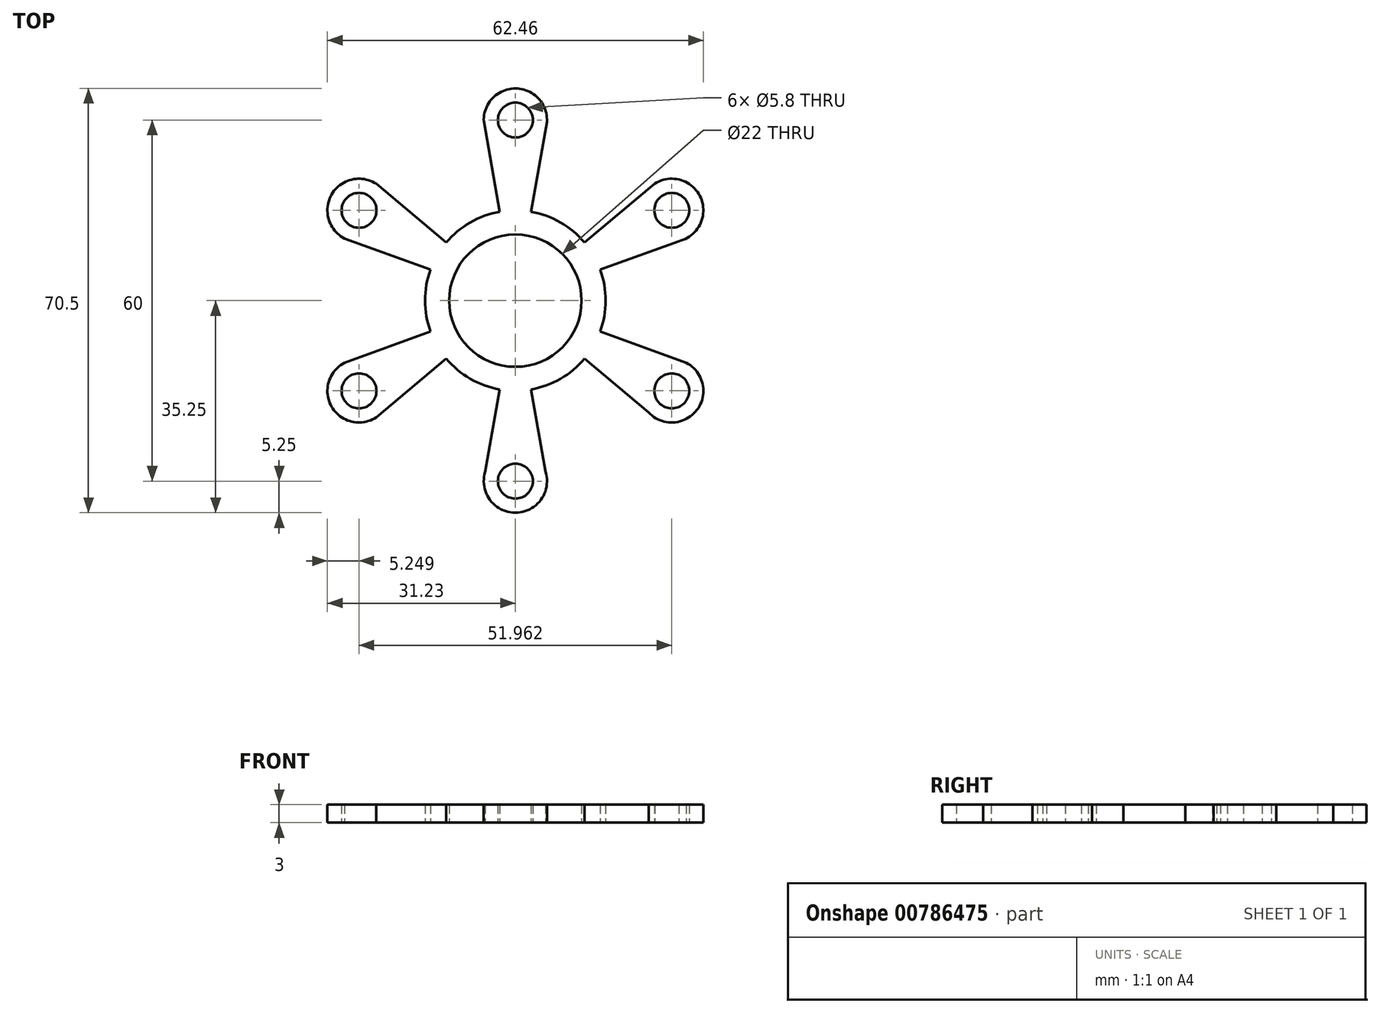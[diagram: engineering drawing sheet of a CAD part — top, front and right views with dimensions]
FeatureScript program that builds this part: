
annotation { "Feature Type Name" : "Feature", "Feature Type Description" : "" }
export const myFeature = defineFeature(function(context is Context, id is Id, definition is map)
    precondition{}
    {
        {
            var Q0;
            Q0=qCreatedBy(makeId("Top.planeOp"),FACE);
            var sketch = newSketch(context, id + "F0", { "sketchPlane" : qUnion([Q0])});
            skArc(sketch, "E0", {"start": v(-2.6, 14.77) * mm, "mid": v(-5.13, 14.1) * mm, "end": v(-7.5, 13) * mm});
            skLineSegment(sketch, "E1", {"start": v(2.6, 14.77) * mm, "end": v(5.25, 29.75) * mm});
            skArc(sketch, "E2", {"start": v(5.25, 29.75) * mm, "mid": v(0, 35.25) * mm, "end": v(-5.25, 29.75) * mm});
            skLineSegment(sketch, "E3.trimOffspring", {"start": v(-2.6, 14.77) * mm, "end": v(-5.25, 29.75) * mm});
            skArc(sketch, "E4.trimOffspring", {"start": v(7.5, 13) * mm, "mid": v(5.13, 14.1) * mm, "end": v(2.6, 14.77) * mm});
            skArc(sketch, "E5.1.0", {"start": v(-23.14, 19.42) * mm, "mid": v(-30.53, 17.63) * mm, "end": v(-28.38, 10.33) * mm});
            skLineSegment(sketch, "E5.1.1", {"start": v(-11.5, 9.64) * mm, "end": v(-23.14, 19.42) * mm});
            skArc(sketch, "E5.1.2", {"start": v(-7.5, 13) * mm, "mid": v(-9.64, 11.5) * mm, "end": v(-11.5, 9.64) * mm});
            skLineSegment(sketch, "E5.1.3", {"start": v(-14.1, 5.13) * mm, "end": v(-28.38, 10.33) * mm});
            skArc(sketch, "E5.1.4", {"start": v(-14.1, 5.13) * mm, "mid": v(-14.77, 2.6) * mm, "end": v(-15, 0) * mm});
            skArc(sketch, "E5.2.0", {"start": v(-28.38, -10.33) * mm, "mid": v(-30.53, -17.63) * mm, "end": v(-23.14, -19.42) * mm});
            skLineSegment(sketch, "E5.2.1", {"start": v(-14.1, -5.13) * mm, "end": v(-28.38, -10.33) * mm});
            skArc(sketch, "E5.2.2", {"start": v(-15, 0) * mm, "mid": v(-14.77, -2.6) * mm, "end": v(-14.1, -5.13) * mm});
            skLineSegment(sketch, "E5.2.3", {"start": v(-11.5, -9.64) * mm, "end": v(-23.14, -19.42) * mm});
            skArc(sketch, "E5.2.4", {"start": v(-11.5, -9.64) * mm, "mid": v(-9.64, -11.5) * mm, "end": v(-7.5, -13) * mm});
            skArc(sketch, "E5.3.0", {"start": v(-5.02, -28.44) * mm, "mid": v(0, -35.25) * mm, "end": v(5.02, -28.44) * mm});
            skLineSegment(sketch, "E5.3.1", {"start": v(-2.6, -14.77) * mm, "end": v(-5.02, -28.44) * mm});
            skArc(sketch, "E5.3.2", {"start": v(-7.5, -13) * mm, "mid": v(-5.13, -14.1) * mm, "end": v(-2.6, -14.77) * mm});
            skLineSegment(sketch, "E5.3.3", {"start": v(2.6, -14.77) * mm, "end": v(5.02, -28.44) * mm});
            skArc(sketch, "E5.3.4", {"start": v(2.6, -14.77) * mm, "mid": v(5.13, -14.1) * mm, "end": v(7.5, -13) * mm});
            skArc(sketch, "E5.4.0", {"start": v(22.13, -18.57) * mm, "mid": v(30.16, -18.18) * mm, "end": v(28.38, -10.33) * mm});
            skLineSegment(sketch, "E5.4.1", {"start": v(11.5, -9.64) * mm, "end": v(22.13, -18.57) * mm});
            skArc(sketch, "E5.4.2", {"start": v(7.5, -13) * mm, "mid": v(9.64, -11.5) * mm, "end": v(11.5, -9.64) * mm});
            skLineSegment(sketch, "E5.4.3", {"start": v(14.1, -5.13) * mm, "end": v(28.38, -10.33) * mm});
            skArc(sketch, "E5.4.4", {"start": v(14.1, -5.13) * mm, "mid": v(14.77, -2.6) * mm, "end": v(15, 0) * mm});
            skArc(sketch, "E5.5.0", {"start": v(27.14, 9.88) * mm, "mid": v(30.82, 17.03) * mm, "end": v(23.14, 19.42) * mm});
            skLineSegment(sketch, "E5.5.1", {"start": v(14.1, 5.13) * mm, "end": v(27.14, 9.88) * mm});
            skArc(sketch, "E5.5.2", {"start": v(15, 0) * mm, "mid": v(14.77, 2.6) * mm, "end": v(14.1, 5.13) * mm});
            skLineSegment(sketch, "E5.5.3", {"start": v(11.5, 9.64) * mm, "end": v(23.14, 19.42) * mm});
            skArc(sketch, "E5.5.4", {"start": v(11.5, 9.64) * mm, "mid": v(9.64, 11.5) * mm, "end": v(7.5, 13) * mm});
            skCircle(sketch, "E6", {"center": v(0, 0) * mm, "radius": 11 * mm});
            skCircle(sketch, "E7", {"center": v(0, -30) * mm, "radius": 2.9 * mm});
            skCircle(sketch, "E8", {"center": v(-25.98, -15) * mm, "radius": 2.9 * mm});
            skCircle(sketch, "E9", {"center": v(-25.98, 15) * mm, "radius": 2.9 * mm});
            skCircle(sketch, "E10", {"center": v(0, 30) * mm, "radius": 2.9 * mm});
            skCircle(sketch, "E11", {"center": v(25.98, 15) * mm, "radius": 2.9 * mm});
            skCircle(sketch, "E12", {"center": v(25.98, -15) * mm, "radius": 2.9 * mm});
            skPoint(sketch, "E13.orphan", {"position": v(-5.25, -29.75) * mm});
            skPoint(sketch, "E14.orphan", {"position": v(5.25, -29.75) * mm});
            skPoint(sketch, "E15.orphan", {"position": v(23.14, -19.42) * mm});
            skPoint(sketch, "E16.orphan", {"position": v(28.38, 10.33) * mm});
            skSolve(sketch);
        }
        {
            var Q0;
            Q0 = qSketchRegion(id + "F0", true);
            extrude(context, id + "F1", {"entities" : qUnion([Q0]), "depth" : 3 * mm, "offsetDistance" : 25 * mm});
        }
    });
